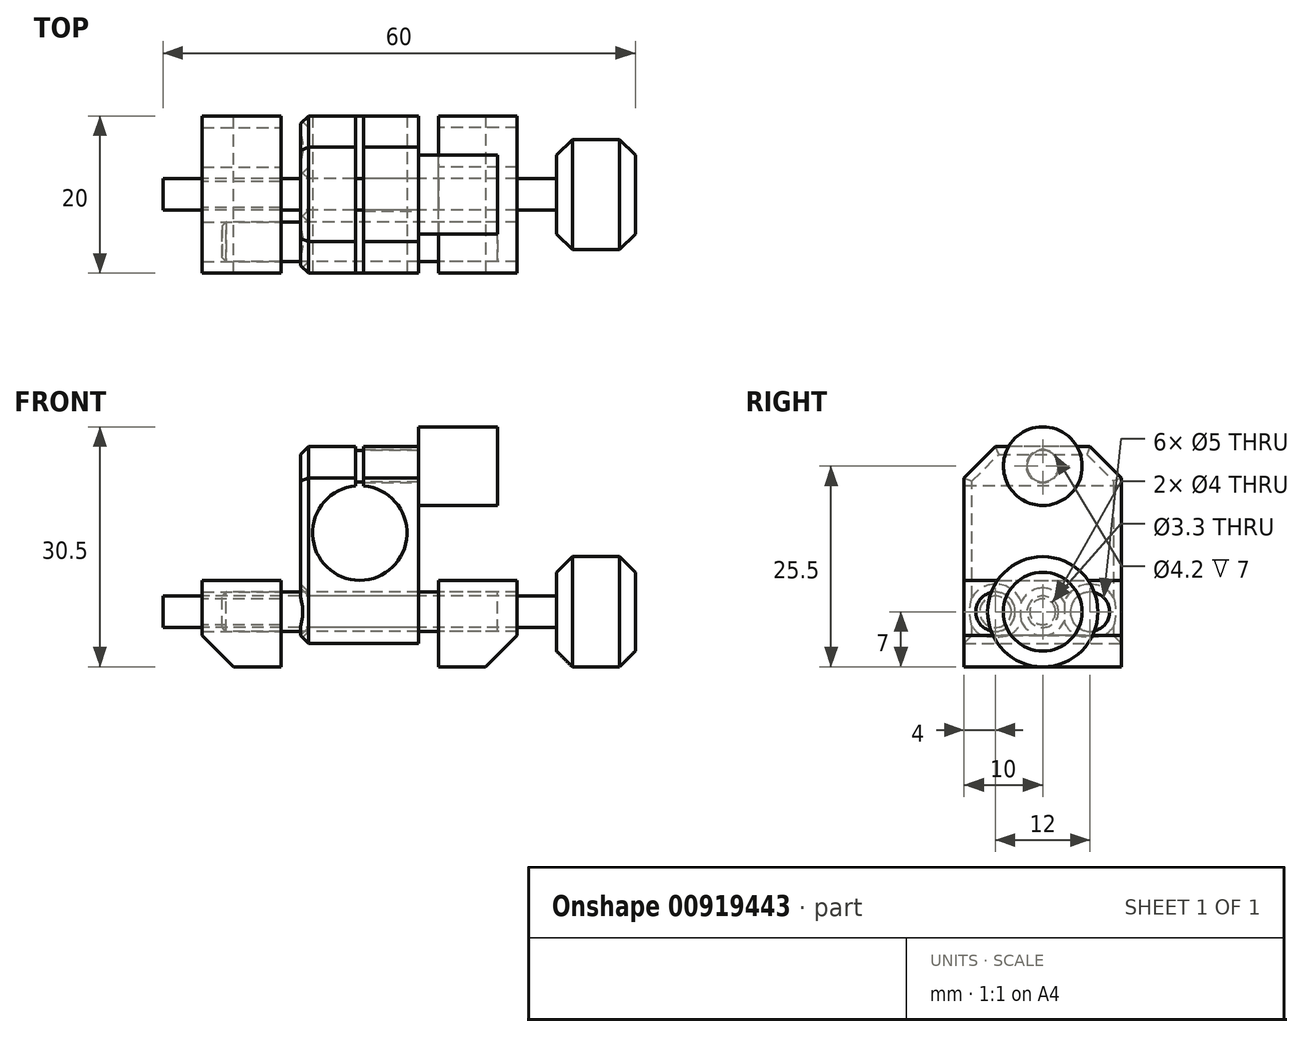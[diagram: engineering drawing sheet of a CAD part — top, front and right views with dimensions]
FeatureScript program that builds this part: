
annotation { "Feature Type Name" : "Feature", "Feature Type Description" : "" }
export const myFeature = defineFeature(function(context is Context, id is Id, definition is map)
    precondition{}
    {
        {
            var Q0;
            Q0=qCreatedBy(makeId("Front.planeOp"),FACE);
            var sketch = newSketch(context, id + "F0", { "sketchPlane" : qUnion([Q0])});
            skLineSegment(sketch, "E0.bottom", {"start": v(-7.5, 25) * mm, "end": v(-0.5, 25) * mm});
            skLineSegment(sketch, "E0.top", {"start": v(-7.5, 0) * mm, "end": v(7.5, 0) * mm});
            skLineSegment(sketch, "E0.left", {"start": v(-7.5, 25) * mm, "end": v(-7.5, 0) * mm});
            skLineSegment(sketch, "E0.right", {"start": v(7.5, 25) * mm, "end": v(7.5, 0) * mm});
            skArc(sketch, "E1", {"start": v(-0.5, 19.98) * mm, "mid": v(0, 8) * mm, "end": v(0.5, 19.98) * mm});
            skLineSegment(sketch, "E2.left", {"start": v(-0.5, 19.98) * mm, "end": v(-0.5, 25) * mm});
            skLineSegment(sketch, "E2.right", {"start": v(0.5, 19.98) * mm, "end": v(0.5, 25) * mm});
            skLineSegment(sketch, "E3.trimOffspring", {"start": v(0.5, 25) * mm, "end": v(7.5, 25) * mm});
            skSolve(sketch);
        }
        {
            var Q0;
            Q0 = qSketchRegion(id + "F0", true);
            extrude(context, id + "F1", {"entities" : qUnion([Q0]), "oppositeDirection" : true, "depth" : 20 * mm, "offsetDistance" : 25 * mm});
        }
        {
            var Q0;
            Q0=qCreatedBy(makeId("Right.planeOp"),FACE);
            var sketch = newSketch(context, id + "F2", { "sketchPlane" : qUnion([Q0])});
            skCircle(sketch, "E4", {"center": v(4, 4) * mm, "radius": 2.5 * mm});
            skCircle(sketch, "E5", {"center": v(16, 4) * mm, "radius": 2.5 * mm});
            skCircle(sketch, "E6", {"center": v(10, 4) * mm, "radius": 2 * mm});
            skLineSegment(sketch, "E7", {"start": v(4, 4) * mm, "end": v(16, 4) * mm, "construction": true});
            skLineSegment(sketch, "E8.bottom", {"start": v(0, 8) * mm, "end": v(20, 8) * mm});
            skLineSegment(sketch, "E8.top", {"start": v(0, -3) * mm, "end": v(20, -3) * mm});
            skLineSegment(sketch, "E8.left", {"start": v(0, 8) * mm, "end": v(0, -3) * mm});
            skLineSegment(sketch, "E8.right", {"start": v(20, 8) * mm, "end": v(20, -3) * mm});
            skSolve(sketch);
        }
        {
            var Q0;
            Q0=makeQuery(id+"F2.imprint","IMPRINT",FACE,{"disambiguationData":[TD([[makeQuery(id+"F2.imprint","IMPRINT",EDGE,{"derivedFrom":sQuery(id+"F2.wireOp",EDGE,"E4")}),1.0]])]});
            var Q1;
            Q1=makeQuery(id+"F2.imprint","IMPRINT",FACE,{"disambiguationData":[TD([[makeQuery(id+"F2.imprint","IMPRINT",EDGE,{"derivedFrom":sQuery(id+"F2.wireOp",EDGE,"E6")}),1.0]])]});
            var Q2;
            Q2=makeQuery(id+"F2.imprint","IMPRINT",FACE,{"disambiguationData":[TD([[makeQuery(id+"F2.imprint","IMPRINT",EDGE,{"derivedFrom":sQuery(id+"F2.wireOp",EDGE,"E5")}),1.0]])]});
            extrude(context, id + "F3", {"entities" : qUnion([Q0, Q1, Q2]), "operationType" : NewBodyOperationType.REMOVE, "endBound" : BoundingType.THROUGH_ALL, "depth" : 50 * mm, "offsetDistance" : 25 * mm, "hasSecondDirection" : true, "secondDirectionBound" : BoundingType.THROUGH_ALL, "secondDirectionOppositeDirection" : true, "secondDirectionDepth" : 25 * mm});
        }
        {
            var Q0;
            Q0=makeQuery(id+"F2.imprint","IMPRINT",FACE,{"disambiguationData":[TD([[makeQuery(id+"F2.imprint","IMPRINT",EDGE,{"derivedFrom":sQuery(id+"F2.wireOp",EDGE,"E4")}),1.0]])]});
            extrude(context, id + "F4", {"entities" : qUnion([Q0]), "depth" : 35 * mm, "offsetDistance" : 25 * mm, "symmetric" : true});
        }
        {
            var Q0;
            Q0 = qSketchRegion(id + "F2", true);
            var Q1;
            Q1=makeQuery(id+"F1.opExtrude","SWEPT_FACE",FACE,{"disambiguationData":[OSD([sQuery(id+"F0.wireOp",EDGE,"E0.right")])]});
            extrude(context, id + "F5", {"entities" : qUnion([Q0]), "depth" : 20 * mm, "endBoundEntityFace" : qUnion([Q1]), "offsetDistance" : 25 * mm, "hasSecondDirection" : true, "secondDirectionOppositeDirection" : false, "secondDirectionDepth" : 10 * mm});
        }
        {
            var Q0;
            Q0=makeQuery(id+"F2.imprint","IMPRINT",FACE,{"disambiguationData":[TD([[makeQuery(id+"F2.imprint","IMPRINT",EDGE,{"derivedFrom":sQuery(id+"F2.wireOp",EDGE,"E4")}),-1.0]])]});
            var Q1;
            Q1=makeQuery(id+"F2.imprint","IMPRINT",FACE,{"disambiguationData":[TD([[makeQuery(id+"F2.imprint","IMPRINT",EDGE,{"derivedFrom":sQuery(id+"F2.wireOp",EDGE,"E6")}),1.0]])]});
            extrude(context, id + "F6", {"entities" : qUnion([Q0, Q1]), "oppositeDirection" : true, "depth" : 20 * mm, "offsetDistance" : 25 * mm, "hasSecondDirection" : true, "secondDirectionOppositeDirection" : true, "secondDirectionDepth" : 10 * mm});
        }
        {
            var Q0;
            Q0=sQuery(id+"F2.wireOp",VERTEX,"E6.center");
            var Q1;
            Q1=makeQuery(id+"F6.opExtrude","SWEPT_BODY",BODY,{"disambiguationData":[OSD([sQuery(id+"F2.wireOp",EDGE,"E4"),sQuery(id+"F2.wireOp",EDGE,"E5"),sQuery(id+"F2.wireOp",EDGE,"E8.bottom"),sQuery(id+"F2.wireOp",EDGE,"E8.top"),sQuery(id+"F2.wireOp",EDGE,"E8.left"),sQuery(id+"F2.wireOp",EDGE,"E8.right")])]});
            hole(context, id + "F7", {"style" : HoleStyle.SIMPLE, "endStyle" : HoleEndStyle.THROUGH, "standardTappedOrClearance" : lookupTablePath({ "standard" : "ISO", "engagement" : "75%", "pitch" : "0.7 mm", "size" : "M4", "type" : "Tapped" }), "standardBlindInLast" : lookupTablePath({ "standard" : "ISO", "engagement" : "75%", "pitch" : "0.7 mm", "size" : "M4", "type" : "Tapped" }), "holeDiameter" : 3.3 * mm, "majorDiameter" : 4 * mm, "showTappedDepth" : true, "isTappedThrough" : true, "tappedDepth" : 16.6 * mm, "tapClearance" : 3, "locations" : qUnion([Q0]), "scope" : qUnion([Q1]), "startStyle" : HoleStartStyle.SKETCH});
        }
        {
            var Q0;
            Q0=makeQuery(id+"F5.opExtrude","CAP_EDGE",EDGE,{"disambiguationData":[OSD([sQuery(id+"F2.wireOp",EDGE,"E8.top")])],"isStart":false});
            var Q1;
            Q1=makeQuery(id+"F6.opExtrude","CAP_EDGE",EDGE,{"disambiguationData":[OSD([sQuery(id+"F2.wireOp",EDGE,"E8.top")])],"isStart":false});
            chamfer(context, id + "F8", {"entities" : qUnion([Q0, Q1]), "width" : 4 * mm, "tangentPropagation" : true});
        }
        {
            var Q0;
            Q0=makeQuery(id+"F1.opExtrude","CAP_EDGE",EDGE,{"disambiguationData":[OSD([sQuery(id+"F0.wireOp",EDGE,"E3.trimOffspring")])],"isStart":true});
            var Q1;
            Q1=makeQuery(id+"F1.opExtrude","CAP_EDGE",EDGE,{"disambiguationData":[OSD([sQuery(id+"F0.wireOp",EDGE,"E0.bottom")])],"isStart":true});
            var Q2;
            Q2=makeQuery(id+"F1.opExtrude","CAP_EDGE",EDGE,{"disambiguationData":[OSD([sQuery(id+"F0.wireOp",EDGE,"E0.bottom")])],"isStart":false});
            var Q3;
            Q3=makeQuery(id+"F1.opExtrude","CAP_EDGE",EDGE,{"disambiguationData":[OSD([sQuery(id+"F0.wireOp",EDGE,"E3.trimOffspring")])],"isStart":false});
            chamfer(context, id + "F9", {"entities" : qUnion([Q0, Q1, Q2, Q3]), "width" : 4 * mm, "tangentPropagation" : true});
        }
        {
            var Q0;
            Q0=makeQuery(id+"F2.imprint","IMPRINT",FACE,{"disambiguationData":[TD([[makeQuery(id+"F2.imprint","IMPRINT",EDGE,{"derivedFrom":sQuery(id+"F2.wireOp",EDGE,"E6")}),1.0]])]});
            extrude(context, id + "F10", {"entities" : qUnion([Q0]), "depth" : 50 * mm, "offsetDistance" : 25 * mm, "symmetric" : true});
        }
        {
            var Q0;
            Q0=makeQuery(id+"F10.opExtrude","CAP_FACE",FACE,{"disambiguationData":[OSD([sQuery(id+"F2.wireOp",EDGE,"E6")])],"isStart":false});
            var sketch = newSketch(context, id + "F11", { "sketchPlane" : qUnion([Q0])});
            skCircle(sketch, "E9", {"center": v(10, 4) * mm, "radius": 7 * mm});
            skSolve(sketch);
        }
        {
            var Q0;
            Q0 = qSketchRegion(id + "F11", true);
            extrude(context, id + "F12", {"entities" : qUnion([Q0]), "operationType" : NewBodyOperationType.ADD, "depth" : 10 * mm, "offsetDistance" : 25 * mm});
        }
        {
            var Q0;
            Q0=qCreatedBy(makeId("Right.planeOp"),FACE);
            var sketch = newSketch(context, id + "F13", { "sketchPlane" : qUnion([Q0])});
            skPoint(sketch, "E10", {"position": v(10, 22.5) * mm});
            skSolve(sketch);
        }
        {
            var Q0;
            Q0=sQuery(id+"F13.wireOp",VERTEX,"E10");
            var Q1;
            Q1=makeQuery(id+"F1.opExtrude","SWEPT_BODY",BODY,{"disambiguationData":[OSD([sQuery(id+"F0.wireOp",EDGE,"E0.bottom"),sQuery(id+"F0.wireOp",EDGE,"E0.top"),sQuery(id+"F0.wireOp",EDGE,"E0.left"),sQuery(id+"F0.wireOp",EDGE,"E0.right"),sQuery(id+"F0.wireOp",EDGE,"E1"),sQuery(id+"F0.wireOp",EDGE,"E2.left"),sQuery(id+"F0.wireOp",EDGE,"E2.right"),sQuery(id+"F0.wireOp",EDGE,"E3.trimOffspring")])]});
            hole(context, id + "F14", {"style" : HoleStyle.SIMPLE, "endStyle" : HoleEndStyle.THROUGH, "standardTappedOrClearance" : lookupTablePath({ "standard" : "ISO", "engagement" : "75%", "pitch" : "0.7 mm", "size" : "M4", "type" : "Tapped" }), "standardBlindInLast" : lookupTablePath({ "standard" : "ISO", "engagement" : "75%", "pitch" : "0.7 mm", "size" : "M4", "type" : "Tapped" }), "holeDiameter" : 3.3 * mm, "majorDiameter" : 4 * mm, "showTappedDepth" : true, "isTappedThrough" : true, "tappedDepth" : 16.6 * mm, "tapClearance" : 3, "locations" : qUnion([Q0]), "scope" : qUnion([Q1]), "startStyle" : HoleStartStyle.SKETCH});
        }
        {
            var Q0;
            Q0=sQuery(id+"F13.wireOp",VERTEX,"E10");
            var Q1;
            Q1=makeQuery(id+"F1.opExtrude","SWEPT_BODY",BODY,{"disambiguationData":[OSD([sQuery(id+"F0.wireOp",EDGE,"E0.bottom"),sQuery(id+"F0.wireOp",EDGE,"E0.top"),sQuery(id+"F0.wireOp",EDGE,"E0.left"),sQuery(id+"F0.wireOp",EDGE,"E0.right"),sQuery(id+"F0.wireOp",EDGE,"E1"),sQuery(id+"F0.wireOp",EDGE,"E2.left"),sQuery(id+"F0.wireOp",EDGE,"E2.right"),sQuery(id+"F0.wireOp",EDGE,"E3.trimOffspring")])]});
            hole(context, id + "F15", {"style" : HoleStyle.SIMPLE, "endStyle" : HoleEndStyle.THROUGH, "oppositeDirection" : true, "holeDiameter" : 4.2 * mm, "majorDiameter" : 4 * mm, "isTappedThrough" : true, "tappedDepth" : 16.6 * mm, "tapClearance" : 3, "locations" : qUnion([Q0]), "scope" : qUnion([Q1]), "startStyle" : HoleStartStyle.SKETCH});
        }
        {
            var Q0;
            Q0=makeQuery(id+"F4.opExtrude","CAP_FACE",FACE,{"disambiguationData":[OSD([sQuery(id+"F2.wireOp",EDGE,"E4")])],"isStart":true});
            chamfer(context, id + "F16", {"entities" : qUnion([Q0]), "width" : 0.5 * mm, "tangentPropagation" : true});
        }
        {
            var Q0;
            Q0=makeQuery(id+"F1.opExtrude","SWEPT_FACE",FACE,{"disambiguationData":[OSD([sQuery(id+"F0.wireOp",EDGE,"E0.left")])]});
            var sketch = newSketch(context, id + "F17", { "sketchPlane" : qUnion([Q0])});
            skCircle(sketch, "E11", {"center": v(-10, 22.5) * mm, "radius": 2 * mm});
            skSolve(sketch);
        }
        {
            var Q0;
            Q0 = qSketchRegion(id + "F17", true);
            var Q1;
            Q1=makeQuery(id+"F1.opExtrude","SWEPT_FACE",FACE,{"disambiguationData":[OSD([sQuery(id+"F0.wireOp",EDGE,"E0.right")])]});
            extrude(context, id + "F18", {"entities" : qUnion([Q0]), "endBound" : BoundingType.UP_TO_SURFACE, "oppositeDirection" : true, "depth" : 20 * mm, "endBoundEntityFace" : qUnion([Q1]), "offsetDistance" : 25 * mm});
        }
        {
            var Q0;
            Q0=makeQuery(id+"F18.opExtrude","CAP_FACE",FACE,{"disambiguationData":[OSD([sQuery(id+"F17.wireOp",EDGE,"E11")])],"isStart":false});
            var sketch = newSketch(context, id + "F19", { "sketchPlane" : qUnion([Q0])});
            skCircle(sketch, "E12", {"center": v(10, 22.5) * mm, "radius": 5 * mm});
            skSolve(sketch);
        }
        {
            var Q0;
            Q0 = qSketchRegion(id + "F19", true);
            extrude(context, id + "F20", {"entities" : qUnion([Q0]), "operationType" : NewBodyOperationType.ADD, "depth" : 10 * mm, "offsetDistance" : 25 * mm});
        }
        {
            var Q0;
            Q0=makeQuery(id+"F12.opExtrude","SWEPT_FACE",FACE,{"disambiguationData":[OSD([sQuery(id+"F11.wireOp",EDGE,"E9")])]});
            var Q1;
            Q1=makeQuery(id+"F20.opExtrude","SWEPT_FACE",FACE,{"disambiguationData":[OSD([sQuery(id+"F19.wireOp",EDGE,"E12")])]});
            chamfer(context, id + "F21", {"entities" : qUnion([Q0, Q1]), "width" : 2 * mm, "tangentPropagation" : true});
        }
        {
            var Q0;
            Q0=makeQuery(id+"F18.opExtrude","CAP_FACE",FACE,{"disambiguationData":[OSD([sQuery(id+"F17.wireOp",EDGE,"E11")])],"isStart":true});
            chamfer(context, id + "F22", {"entities" : qUnion([Q0]), "width" : 1 * mm, "tangentPropagation" : true});
        }
    });
